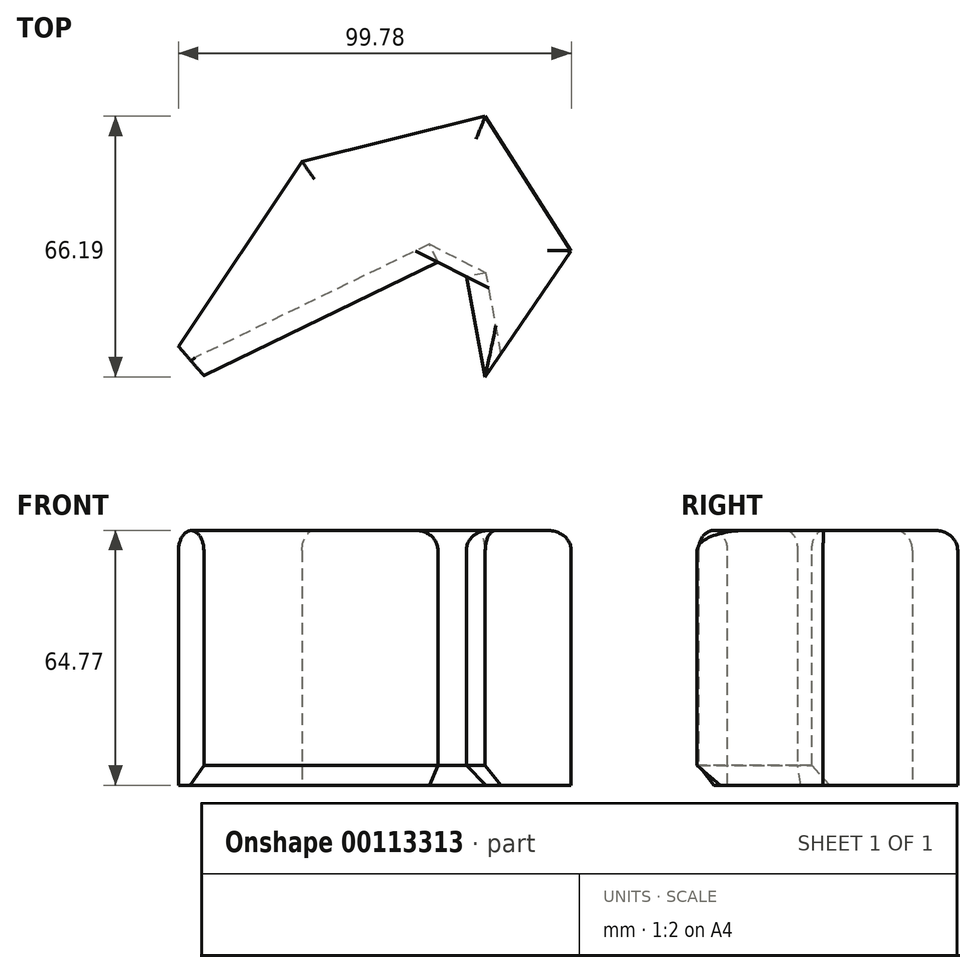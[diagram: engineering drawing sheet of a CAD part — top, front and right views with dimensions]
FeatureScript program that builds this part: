
annotation { "Feature Type Name" : "Feature", "Feature Type Description" : "" }
export const myFeature = defineFeature(function(context is Context, id is Id, definition is map)
    precondition{}
    {
        {
            var Q0;
            Q0=qCreatedBy(makeId("Top.planeOp"),FACE);
            var sketch = newSketch(context, id + "F0", { "sketchPlane" : qUnion([Q0])});
            skLineSegment(sketch, "E0", {"start": v(-82.28, -39.83) * mm, "end": v(-40.5, 22.67) * mm});
            skLineSegment(sketch, "E1", {"start": v(-40.5, 22.67) * mm, "end": v(6.03, 34.19) * mm});
            skLineSegment(sketch, "E2", {"start": v(6.03, 34.19) * mm, "end": v(27.88, 0) * mm});
            skLineSegment(sketch, "E3", {"start": v(27.88, 0) * mm, "end": v(6.03, -32) * mm});
            skLineSegment(sketch, "E4", {"start": v(6.03, -32) * mm, "end": v(0, 0) * mm});
            skLineSegment(sketch, "E5", {"start": v(0, 0) * mm, "end": v(-82.28, -39.83) * mm});
            skSolve(sketch);
        }
        {
            var Q0;
            Q0=makeQuery(id+"F0.imprint","IMPRINT",FACE,{"disambiguationData":[TD([[makeQuery(id+"F0.imprint","IMPRINT",EDGE,{"derivedFrom":sQuery(id+"F0.wireOp",EDGE,"E0")}),-1.0]])]});
            extrude(context, id + "F1", {"entities" : qUnion([Q0]), "depth" : 64.77 * mm});
        }
        {
            var Q0;
            Q0=makeQuery(id+"F1.opExtrude","CAP_EDGE",EDGE,{"disambiguationData":[OSD([sQuery(id+"F0.wireOp",EDGE,"E5")])],"isStart":false});
            var Q1;
            Q1=makeQuery(id+"F1.opExtrude","CAP_FACE",FACE,{"disambiguationData":[OSD([sQuery(id+"F0.wireOp",EDGE,"E0"),sQuery(id+"F0.wireOp",EDGE,"E1"),sQuery(id+"F0.wireOp",EDGE,"E2"),sQuery(id+"F0.wireOp",EDGE,"E3"),sQuery(id+"F0.wireOp",EDGE,"E4"),sQuery(id+"F0.wireOp",EDGE,"E5")])],"isStart":false});
            fillet(context, id + "F2", {"entities" : qUnion([Q0, Q1]), "radius" : 5.08 * mm, "tangentPropagation" : true, "allowEdgeOverflow" : false});
        }
        {
            var Q0;
            Q0=makeQuery(id+"F1.opExtrude","SWEPT_FACE",FACE,{"disambiguationData":[OSD([sQuery(id+"F0.wireOp",EDGE,"E5")])]});
            chamfer(context, id + "F3", {"entities" : qUnion([Q0]), "width" : 5.08 * mm, "tangentPropagation" : true});
        }
    });
